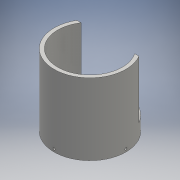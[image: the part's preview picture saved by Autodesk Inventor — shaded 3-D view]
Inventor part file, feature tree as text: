
AUTODESK INVENTOR PART (.ipt)
format: ipt  version: 2016 (Build 200138000, 138)  size: 143,360 bytes
history: native  units: mm
features: extrude x6, sketch x6, other x5
ambient origin geometry x8: Origin, YZ Plane, XZ Plane, XY Plane, X Axis, Y Axis, Z Axis, Center Point
bodies: Body1 (feature_tree)
feature tree (17):
  other  "ソリッド1"
  extrude  "押し出し1"  Depth=90.0mm
  extrude  "押し出し2"  Depth=100.0mm
  other  "作業平面1"
  extrude  "押し出し3"  Depth=20.0mm TaperAngle=0.0deg
  other  "作業平面2"
  other  "作業平面3"
  other  "作業平面4"
  extrude  "押し出し4"  TaperAngle=150.0deg  [1 undecoded]
  extrude  "押し出し5"  TaperAngle=30.0deg  [1 undecoded]
  extrude  "押し出し6"  Depth=80.0mm TaperAngle=0.0deg
  sketch  "スケッチ1"
  sketch  "スケッチ2"
  sketch  "スケッチ3"
  sketch  "スケッチ4"
  sketch  "スケッチ5"
  sketch  "スケッチ6"
note: 2 required parameter values undecoded (feature->parameter linkage not recoverable at this tier; creation-order binding heuristic only, values carry confidence <= 0.55)
